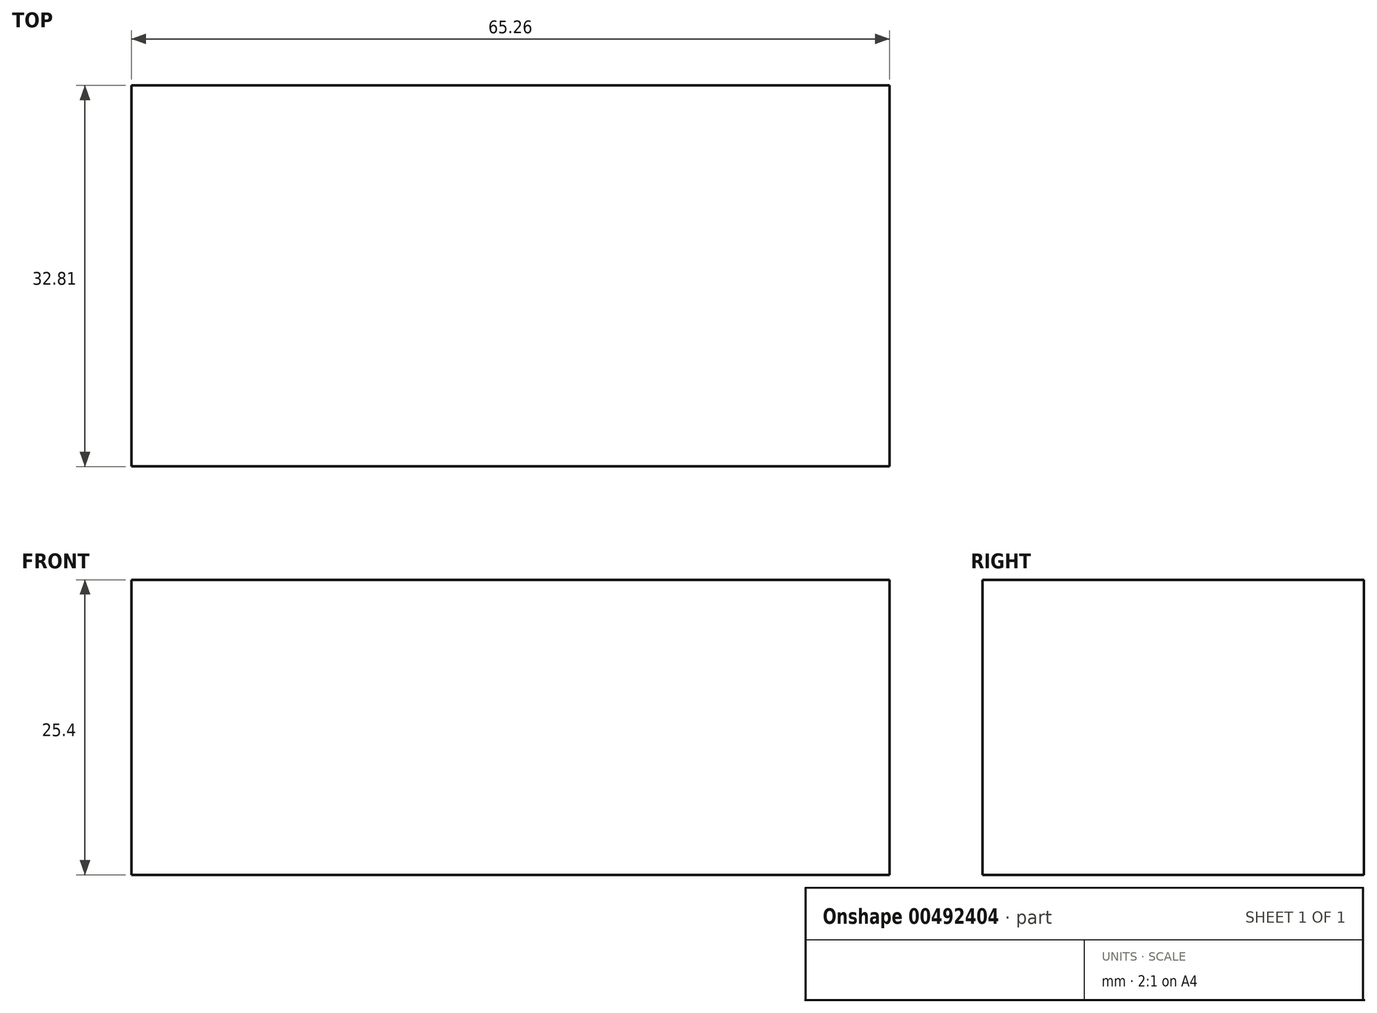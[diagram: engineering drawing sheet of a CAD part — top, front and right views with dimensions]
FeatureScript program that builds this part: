
annotation { "Feature Type Name" : "Feature", "Feature Type Description" : "" }
export const myFeature = defineFeature(function(context is Context, id is Id, definition is map)
    precondition{}
    {
        {
            var Q0;
            Q0=qCreatedBy(makeId("Top.planeOp"),FACE);
            var sketch = newSketch(context, id + "F0", { "sketchPlane" : qUnion([Q0])});
            skLineSegment(sketch, "E0.bottom", {"start": v(-32.64, -15.4) * mm, "end": v(32.62, -15.4) * mm});
            skLineSegment(sketch, "E0.top", {"start": v(-32.64, -48.2) * mm, "end": v(32.62, -48.2) * mm});
            skLineSegment(sketch, "E0.left", {"start": v(-32.64, -15.4) * mm, "end": v(-32.64, -48.2) * mm});
            skLineSegment(sketch, "E0.right", {"start": v(32.62, -15.4) * mm, "end": v(32.62, -48.2) * mm});
            skSolve(sketch);
        }
        {
            var Q0;
            Q0 = qSketchRegion(id + "F0", true);
            extrude(context, id + "F1", {"entities" : qUnion([Q0]), "depth" : 25.4 * mm});
        }
    });
